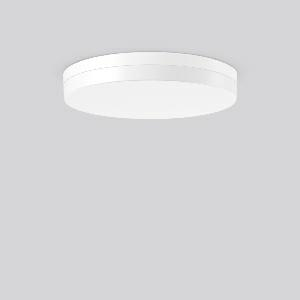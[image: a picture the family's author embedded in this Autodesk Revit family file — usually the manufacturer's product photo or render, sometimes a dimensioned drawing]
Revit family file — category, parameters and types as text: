
# Revit family: flat_slim_round_312633_002_19_3407
name_source: partatom
category: Lighting Fixtures
units: mm (PartAtom-declared; Revit-internal decimal feet)

## family parameters
Cut with Voids When Loaded = No
Host = Face
Light Source = No
Part Type = Normal
Room Calculation Point = No
Round Connector Dimension = Use Diameter
Shared = No

## types (1)
- MultiLumen 1 830 (1 x LED Modul 830, 3350 lm, 3000)
    Apparent Load = 31 VA
    CIE Flux Codes = 41 71 90 86 100
    Color Rendering = 80
    Color Temperature = 3000
    Default Elevation = 1800 mm
    Height = 75 mm
    Lamp = 1 x LED Modul 830
    Lamp Light Flux = 3350 lm
    Lamp count = 1
    Length = 480 mm
    Lifetime = 50000 h
    Luminous efficacy = 108 lm/W
    Manufacturer = RZB
    ModVariant = No
    Model = 312633.002.19
    Mounting Place = Ceiling
    Mounting Type = Surface mounted
    Number of Poles = 1
    OnlyDefault = Yes
    Power Factor = 1
    Product Name = FLAT SLIM round
    Product group = Surface mounted ceiling and wall luminaires
    ProductGroupID = 305
    Protection Class = Protection class I
    Protection Degree = Degree of protection
    RLX_Detail_Level = 1
    RLX_Emergency_Light_Flux = 0 lm
    RLX_Emergency_Type = 0
    RLX_Emergency_Type_DB = No
    RlxData = <blob elided: 21889 chars, md5=4019e71e>
    Socket = socket
    Standby Power = 0 W
    System Light Flux = 3350 lm
    System Power = 31 W
    Type Comments = MultiLumen 1 830
    Type Image = 312633.002.jpg
    URL = http://relux.com
    VarID = multilumen_1_830
    Voltage = 0 V
    Weight = 0.00 kg
    Width = 0 mm  [stored 0 ft]

note: [stored X ft] marks values corroborated as IEEE doubles in the binary element streams (Revit-internal decimal feet)

## geometry (parser evidence)
native form markers: Blend x4, Sweep x13
no freeform markers — native parametric forms only
